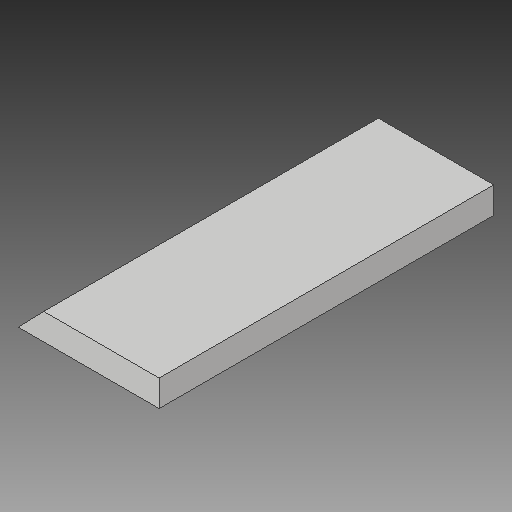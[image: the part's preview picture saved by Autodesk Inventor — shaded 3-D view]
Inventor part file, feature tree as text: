
AUTODESK INVENTOR PART (.ipt)
format: ipt  version: 2017 (Build 210142000, 142)  size: 84,992 bytes
history: native  units: in
note: dims shown in document units (in); Inventor stores cm internally (conversion verified against a paired STEP export)
features: extrude x2, sketch x2
ambient origin geometry x8: Origin, YZ Plane, XZ Plane, XY Plane, X Axis, Y Axis, Z Axis, Center Point
bodies: Solid1 (feature_tree)
feature tree (4):
  extrude  "Extrusion1"  Depth=9.5in
  extrude  "Extrusion2"  Depth=0.75in TaperAngle=0.0deg
  sketch  "Sketch1"  dims[d0=4.0in d1=9.5in]
  sketch  "Sketch2"  dims[d2=0.75in d3=0.0in d4=10.0in d5=0.0in]
